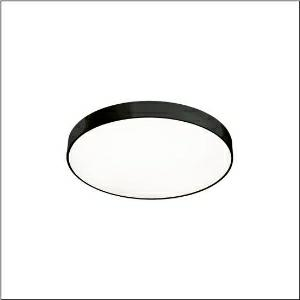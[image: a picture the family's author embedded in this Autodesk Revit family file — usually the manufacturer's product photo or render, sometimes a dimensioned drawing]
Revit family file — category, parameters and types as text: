
# Revit family: round_21_m_51mr36fd0321b
name_source: partatom
category: Lighting Fixtures
units: mm (PartAtom-declared; Revit-internal decimal feet)

## family parameters
Cut with Voids When Loaded = No
Host = Face
Light Source = No
Part Type = Normal
Room Calculation Point = No
Round Connector Dimension = Use Diameter
Shared = No

## types (1)
- Round 21 M (1 x LED, 7500 lm, 54.9 W, 3000K)
    Apparent Load = 55 VA
    CIE Flux Codes = 49 80 96 100 100
    Color Rendering = 80
    Color Temperature = 3000K
    Default Elevation = 1800 mm
    Description = Round 21 M, wall and ceiling luminaire, primary optical cover: cover, of PMMA, opal, light emission: direct distribution, primary light characteristic: symmetric, installation type: suspended mounting, surface-mounted, LED, rated luminous flux: 7.500lm, luminous efficacy: 137lm/W, light colour: 830, colour temperature: 3000K, control gear: DALI 2, with terminal, 5-pole, mains connection: 230V, AC, 50/60Hz, rated input power: 54.8W, housing, of aluminium, coated, black, diameter: 600mm, height: 62mm, protection rating (complete): IP40, insulation class (complete): insulation class I (protective earthing), certification: CE, impact resistance: IK04, permissible operating ambient temperature: -10..+35°C, packaging unit: 1 piece
    Height = 87 mm
    Lamp = 1 x LED
    Lamp Light Flux = 7500 lm
    Lamp Power = 54.9 W
    Lamp count = 1
    Length = 600 mm
    Luminous efficacy = 137 lm/W
    Manufacturer = Siteco
    ModVariant = No
    Model = 51MR36FD0321B
    Mounting Place = Ceiling
    Mounting Type = Surface mounted
    Number of Poles = 1
    OnlyDefault = Yes
    Power Factor = 1
    Product Name = Round 21 M
    Product group = wall and ceiling luminaire | ceiling mounted
    ProductGroupID = 305
    Protection Class = Protection class I
    Protection Degree = IP 40
    RLX_Detail_Level = 1
    RLX_Emergency_Light_Flux = 0 lm
    RLX_Emergency_Type = 0
    RLX_Emergency_Type_DB = No
    RlxData = <blob elided: 17745 chars, md5=f1c4f83b>
    Socket = socket
    Standby Power = 0 W
    System Light Flux = 7500 lm
    System Power = 55 W
    Type Comments = Product without accessories
    Type Image = l_1258332.jpg
    URL = http://relux.com
    VarID = ---
    Voltage = 0 V
    Weight = 0.00 kg
    Width = 0 mm  [stored 0 ft]

note: [stored X ft] marks values corroborated as IEEE doubles in the binary element streams (Revit-internal decimal feet)

## geometry (parser evidence)
native form markers: Blend x4, Sweep x10
no freeform markers — native parametric forms only
